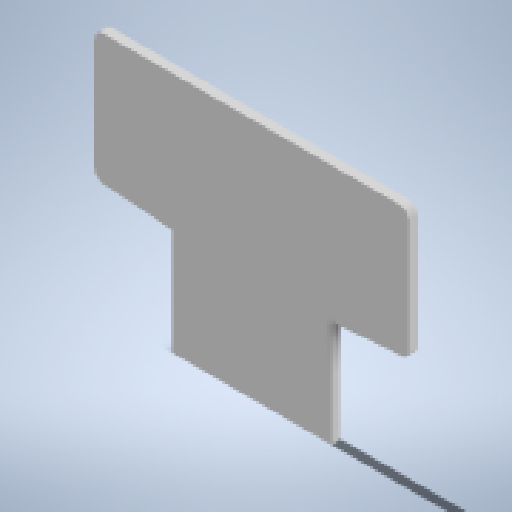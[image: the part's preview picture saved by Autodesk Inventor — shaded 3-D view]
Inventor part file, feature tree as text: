
AUTODESK INVENTOR PART (.ipt)
format: ipt  version: 2023.3 (Build 273359000, 359)  size: 164,352 bytes
history: native  units: mm
features: reference x5, other x3, extrude x2, sketch x2
ambient origin geometry x8: Origin, YZ Plane, XZ Plane, XY Plane, X Axis, Y Axis, Z Axis, Center Point
bodies: Solid1 (feature_tree)
feature tree (12):
  extrude  "Extrusion1"  Depth=0.1mm
  extrude  "Extrusion2"  Depth=0.3mm
  sketch  "Sketch1"  dims[d0=0.1mm d1=0.1mm]
  reference  "Reference1"
  reference  "Reference2"
  reference  "Reference3"
  reference  "Reference4"
  reference  "Reference5"
  sketch  "Sketch2"  dims[d2=0.1mm d3=0.1mm d4=0.1mm d5=0.1mm d6=0.1mm d7=0.1mm d8=0.4mm d9=0.4mm d10=0.4mm d11=0.4mm d12=0.3mm d13=0.0mm d14=2.75mm d15=1.05mm d16=2.5mm d17=2.5mm d18=0.3mm d19=0.0mm]
  parser-record x1  (decoder bookkeeping rows leaked as tree rows — omitted from the tree; the rows remain in map.json)
  other  "np2_full_assembly.iam"
  other  "np2_cap_with_headstage:1"
note: 1 file-system path scrubbed to <path> (originals preserved in map.json)
